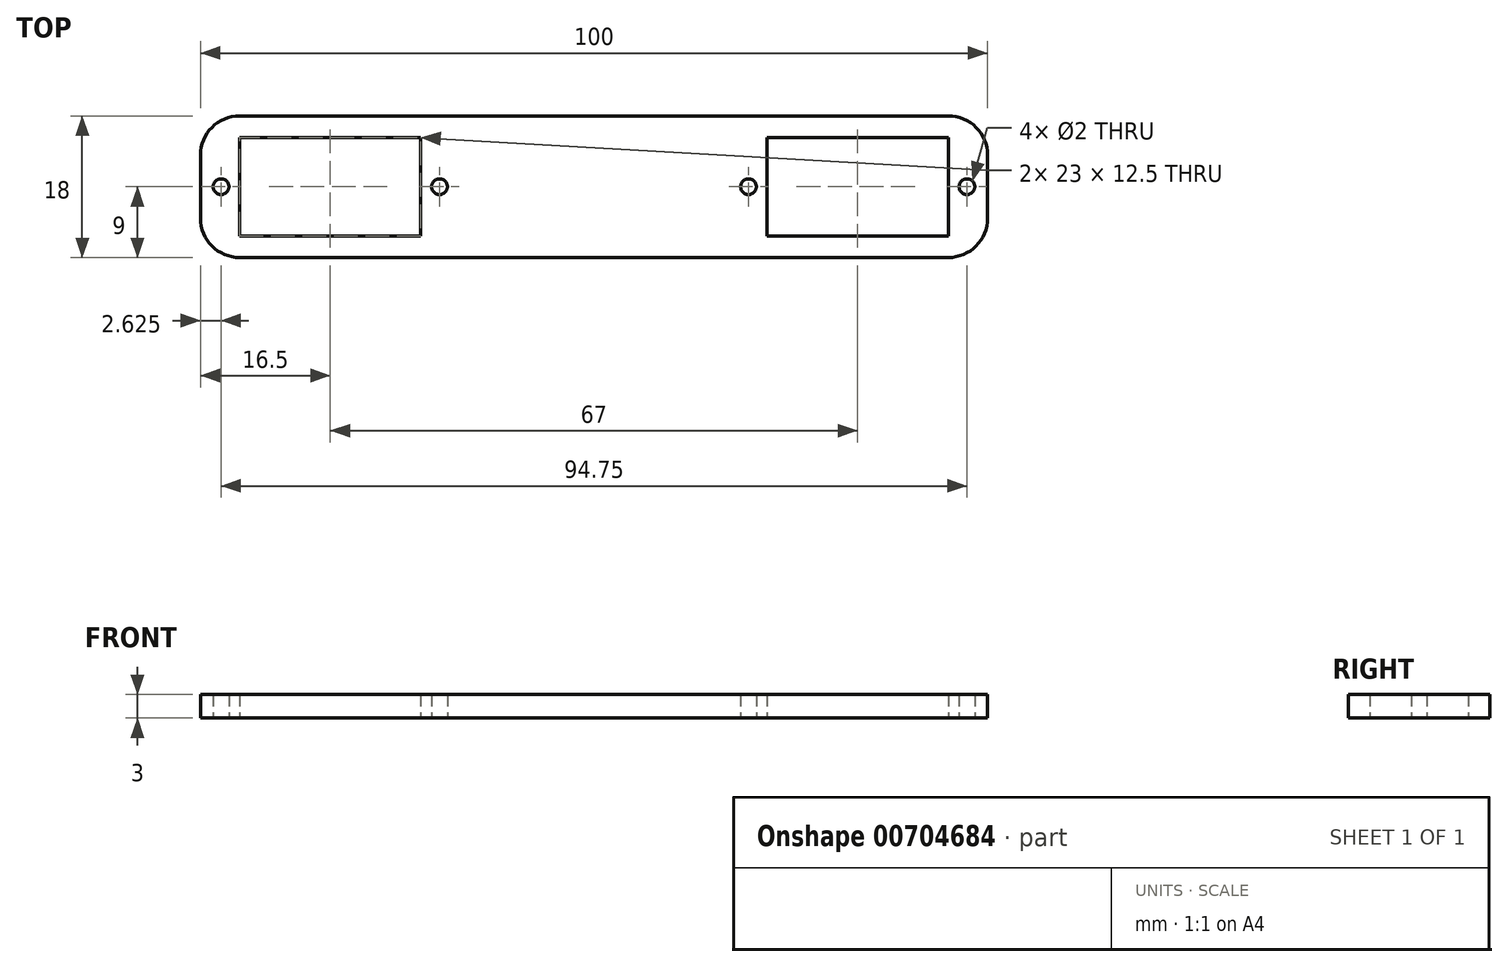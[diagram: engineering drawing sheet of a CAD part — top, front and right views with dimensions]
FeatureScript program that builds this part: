
annotation { "Feature Type Name" : "Feature", "Feature Type Description" : "" }
export const myFeature = defineFeature(function(context is Context, id is Id, definition is map)
    precondition{}
    {
        {
            var Q0;
            Q0=qCreatedBy(makeId("Top.planeOp"),FACE);
            var sketch = newSketch(context, id + "F0", { "sketchPlane" : qUnion([Q0])});
            skLineSegment(sketch, "E0.bottom", {"start": v(-50, 9) * mm, "end": v(50, 9) * mm});
            skLineSegment(sketch, "E0.top", {"start": v(-50, -9) * mm, "end": v(50, -9) * mm});
            skLineSegment(sketch, "E0.left", {"start": v(-50, 9) * mm, "end": v(-50, -9) * mm});
            skLineSegment(sketch, "E0.right", {"start": v(50, 9) * mm, "end": v(50, -9) * mm});
            skLineSegment(sketch, "E1.bottom", {"start": v(-45, 6.25) * mm, "end": v(-22, 6.25) * mm});
            skLineSegment(sketch, "E1.top", {"start": v(-45, -6.25) * mm, "end": v(-22, -6.25) * mm});
            skLineSegment(sketch, "E1.left", {"start": v(-45, 6.25) * mm, "end": v(-45, -6.25) * mm});
            skLineSegment(sketch, "E1.right", {"start": v(-22, 6.25) * mm, "end": v(-22, -6.25) * mm});
            skCircle(sketch, "E2", {"center": v(-19.63, 0) * mm, "radius": 1 * mm});
            skPoint(sketch, "E2.centerSnap0", {"position": v(-22, 0) * mm});
            skCircle(sketch, "E3", {"center": v(-47.38, 0) * mm, "radius": 1 * mm});
            skLineSegment(sketch, "E4.bottom", {"start": v(22, 6.25) * mm, "end": v(45, 6.25) * mm});
            skLineSegment(sketch, "E4.top", {"start": v(22, -6.25) * mm, "end": v(45, -6.25) * mm});
            skLineSegment(sketch, "E4.left", {"start": v(22, 6.25) * mm, "end": v(22, -6.25) * mm});
            skLineSegment(sketch, "E4.right", {"start": v(45, 6.25) * mm, "end": v(45, -6.25) * mm});
            skCircle(sketch, "E5", {"center": v(47.38, 0) * mm, "radius": 1 * mm});
            skPoint(sketch, "E5.centerSnap0", {"position": v(45, 0) * mm});
            skCircle(sketch, "E6", {"center": v(19.63, 0) * mm, "radius": 1 * mm});
            skSolve(sketch);
        }
        {
            var Q0;
            Q0=makeQuery(id+"F0.imprint","IMPRINT",FACE,{"disambiguationData":[TD([[makeQuery(id+"F0.imprint","IMPRINT",EDGE,{"derivedFrom":sQuery(id+"F0.wireOp",EDGE,"E0.bottom")}),-1.0]])]});
            extrude(context, id + "F1", {"entities" : qUnion([Q0]), "depth" : 3 * mm, "offsetDistance" : 25 * mm});
        }
        {
            var Q0;
            Q0=makeQuery(id+"F1.opExtrude","SWEPT_EDGE",EDGE,{"disambiguationData":[OSD([sQuery(id+"F0.wireOp",EDGE,"E0.bottom"),sQuery(id+"F0.wireOp",EDGE,"E0.left")])]});
            var Q1;
            Q1=makeQuery(id+"F1.opExtrude","SWEPT_EDGE",EDGE,{"disambiguationData":[OSD([sQuery(id+"F0.wireOp",EDGE,"E0.top"),sQuery(id+"F0.wireOp",EDGE,"E0.left")])]});
            var Q2;
            Q2=makeQuery(id+"F1.opExtrude","SWEPT_EDGE",EDGE,{"disambiguationData":[OSD([sQuery(id+"F0.wireOp",EDGE,"E0.bottom"),sQuery(id+"F0.wireOp",EDGE,"E0.right")])]});
            var Q3;
            Q3=makeQuery(id+"F1.opExtrude","SWEPT_EDGE",EDGE,{"disambiguationData":[OSD([sQuery(id+"F0.wireOp",EDGE,"E0.top"),sQuery(id+"F0.wireOp",EDGE,"E0.right")])]});
            fillet(context, id + "F2", {"entities" : qUnion([Q0, Q1, Q2, Q3]), "radius" : 5 * mm, "tangentPropagation" : true, "allowEdgeOverflow" : false});
        }
    });
